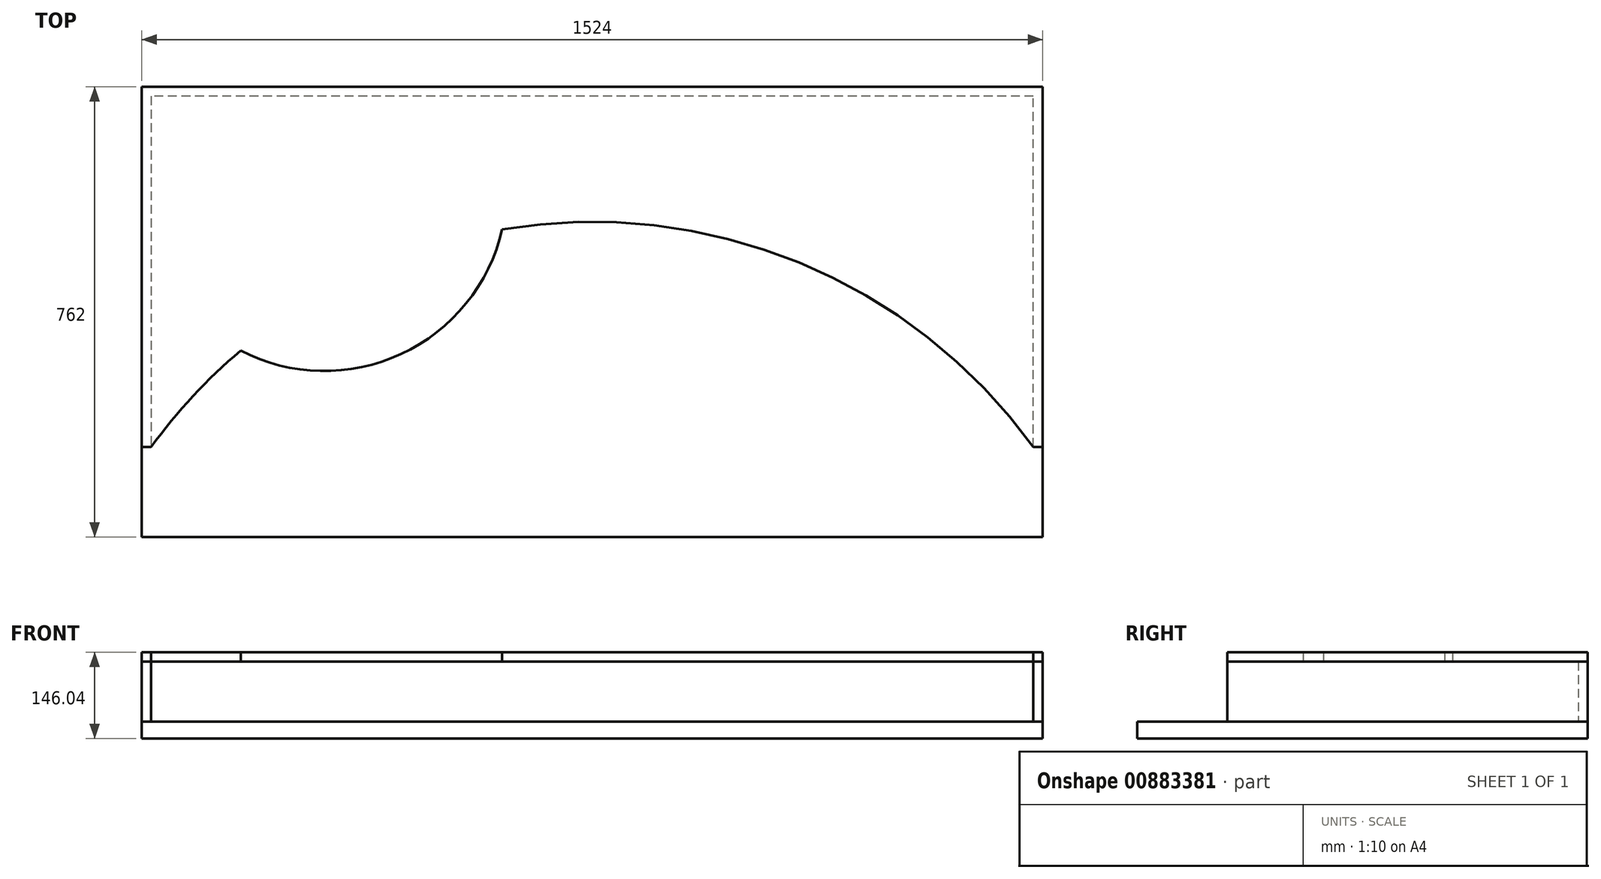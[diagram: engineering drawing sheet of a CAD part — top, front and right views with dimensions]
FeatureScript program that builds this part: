
annotation { "Feature Type Name" : "Feature", "Feature Type Description" : "" }
export const myFeature = defineFeature(function(context is Context, id is Id, definition is map)
    precondition{}
    {
        {
            var Q0;
            Q0=qCreatedBy(makeId("Top.planeOp"),FACE);
            var sketch = newSketch(context, id + "F0", { "sketchPlane" : qUnion([Q0])});
            skLineSegment(sketch, "E0.bottom", {"start": v(762, 381) * mm, "end": v(-762, 381) * mm});
            skLineSegment(sketch, "E0.top", {"start": v(762, -381) * mm, "end": v(-762, -381) * mm});
            skLineSegment(sketch, "E0.left", {"start": v(762, 381) * mm, "end": v(762, -381) * mm});
            skLineSegment(sketch, "E0.right", {"start": v(-762, 381) * mm, "end": v(-762, -381) * mm});
            skPoint(sketch, "E0.middle", {"position": v(0, 0) * mm});
            skSolve(sketch);
        }
        {
            var Q0;
            Q0 = qSketchRegion(id + "F0", true);
            extrude(context, id + "F1", {"entities" : qUnion([Q0]), "oppositeDirection" : true, "depth" : 28.57 * mm, "offsetDistance" : 25.4 * mm});
        }
        {
            var Q0;
            Q0=makeQuery(id+"F1.opExtrude","CAP_FACE",FACE,{"disambiguationData":[OSD([sQuery(id+"F0.wireOp",EDGE,"E0.bottom"),sQuery(id+"F0.wireOp",EDGE,"E0.top"),sQuery(id+"F0.wireOp",EDGE,"E0.left"),sQuery(id+"F0.wireOp",EDGE,"E0.right")])],"isStart":true});
            var sketch = newSketch(context, id + "F2", { "sketchPlane" : qUnion([Q0])});
            skLineSegment(sketch, "E1.bottom", {"start": v(-762, 381) * mm, "end": v(-746.13, 381) * mm});
            skLineSegment(sketch, "E1.top", {"start": v(-762, -228.6) * mm, "end": v(-746.13, -228.6) * mm});
            skLineSegment(sketch, "E1.left", {"start": v(-762, 381) * mm, "end": v(-762, -228.6) * mm});
            skLineSegment(sketch, "E1.right", {"start": v(-746.13, 381) * mm, "end": v(-746.13, -228.6) * mm});
            skLineSegment(sketch, "E2.bottom", {"start": v(762, -228.6) * mm, "end": v(746.12, -228.6) * mm});
            skLineSegment(sketch, "E2.top", {"start": v(762, 381) * mm, "end": v(746.12, 381) * mm});
            skLineSegment(sketch, "E2.left", {"start": v(762, -228.6) * mm, "end": v(762, 381) * mm});
            skLineSegment(sketch, "E2.right", {"start": v(746.13, -228.6) * mm, "end": v(746.12, 381) * mm});
            skLineSegment(sketch, "E3.bottom", {"start": v(746.12, 381) * mm, "end": v(-746.13, 381) * mm});
            skLineSegment(sketch, "E3.top", {"start": v(746.12, 365.12) * mm, "end": v(-746.13, 365.12) * mm});
            skLineSegment(sketch, "E3.left", {"start": v(746.12, 381) * mm, "end": v(746.12, 365.12) * mm});
            skLineSegment(sketch, "E3.right", {"start": v(-746.13, 381) * mm, "end": v(-746.13, 365.12) * mm});
            skSolve(sketch);
        }
        {
            var Q0;
            Q0 = qSketchRegion(id + "F2", true);
            extrude(context, id + "F3", {"entities" : qUnion([Q0]), "depth" : 101.6 * mm, "offsetDistance" : 25.4 * mm});
        }
        {
            var Q0;
            Q0=makeQuery(id+"F3.opExtrude","CAP_FACE",FACE,{"disambiguationData":[OSD([sQuery(id+"F2.wireOp",EDGE,"E1.bottom"),sQuery(id+"F2.wireOp",EDGE,"E1.top"),sQuery(id+"F2.wireOp",EDGE,"E1.left"),sQuery(id+"F2.wireOp",EDGE,"E1.right"),sQuery(id+"F2.wireOp",EDGE,"E2.bottom"),sQuery(id+"F2.wireOp",EDGE,"E2.top"),sQuery(id+"F2.wireOp",EDGE,"E2.left"),sQuery(id+"F2.wireOp",EDGE,"E2.right"),sQuery(id+"F2.wireOp",EDGE,"E3.bottom"),sQuery(id+"F2.wireOp",EDGE,"E3.top")])],"isStart":false});
            var sketch = newSketch(context, id + "F4", { "sketchPlane" : qUnion([Q0])});
            skArc(sketch, "E4", {"start": v(746.12, -228.6) * mm, "mid": v(0, 152.4) * mm, "end": v(-746.13, -228.6) * mm});
            skLineSegment(sketch, "E5.0", {"start": v(762, -381) * mm, "end": v(-762, -381) * mm, "construction": true});
            skLineSegment(sketch, "E6", {"start": v(457.2, -381) * mm, "end": v(457.2, -76.2) * mm, "construction": true});
            skLineSegment(sketch, "E7", {"start": v(-152.4, -381) * mm, "end": v(-152.4, 50.8) * mm, "construction": true});
            skLineSegment(sketch, "E8", {"start": v(-482.6, -381) * mm, "end": v(-482.6, -177.8) * mm, "construction": true});
            skSolve(sketch);
        }
        {
            var Q0;
            Q0=makeQuery(id+"F4.imprint","IMPRINT",FACE,{"disambiguationData":[TD([[makeQuery(id+"F4.imprint","IMPRINT",EDGE,{"derivedFrom":sQuery(id+"F4.wireOp",EDGE,"E4")}),-1.0]])]});
            var Q1;
            Q1=makeQuery(id+"F4.imprint","IMPRINT",FACE,{"disambiguationData":[TD([[makeQuery(id+"F4.imprint","IMPRINT",EDGE,{"derivedFrom":makeQuery(id+"F3.opExtrude","CAP_EDGE",EDGE,{"disambiguationData":[OSD([sQuery(id+"F2.wireOp",EDGE,"E1.top")])],"isStart":false})}),1.0]])]});
            extrude(context, id + "F5", {"entities" : qUnion([Q0, Q1]), "depth" : 15.88 * mm, "offsetDistance" : 25.4 * mm});
        }
        {
            var Q0;
            Q0=makeQuery(id+"F5.opExtrude","CAP_FACE",FACE,{"disambiguationData":[OSD([sQuery(id+"F2.wireOp",EDGE,"E1.bottom"),sQuery(id+"F2.wireOp",EDGE,"E1.top"),sQuery(id+"F2.wireOp",EDGE,"E1.left"),sQuery(id+"F2.wireOp",EDGE,"E2.bottom"),sQuery(id+"F2.wireOp",EDGE,"E2.top"),sQuery(id+"F2.wireOp",EDGE,"E2.left"),sQuery(id+"F2.wireOp",EDGE,"E3.bottom"),sQuery(id+"F4.wireOp",EDGE,"E4")])],"isStart":false});
            var sketch = newSketch(context, id + "F6", { "sketchPlane" : qUnion([Q0])});
            skLineSegment(sketch, "E9.bottom", {"start": v(247.65, 228.6) * mm, "end": v(-247.65, 228.6) * mm});
            skLineSegment(sketch, "E9.top", {"start": v(247.65, 254) * mm, "end": v(-247.65, 254) * mm});
            skLineSegment(sketch, "E9.left", {"start": v(247.65, 228.6) * mm, "end": v(247.65, 254) * mm});
            skLineSegment(sketch, "E9.right", {"start": v(-247.65, 228.6) * mm, "end": v(-247.65, 254) * mm});
            skPoint(sketch, "E9.middle", {"position": v(0, 241.3) * mm});
            skLineSegment(sketch, "E10", {"start": v(247.65, 228.6) * mm, "end": v(700.33, 27.59) * mm});
            skLineSegment(sketch, "E11", {"start": v(700.33, 27.59) * mm, "end": v(710.63, 50.8) * mm});
            skLineSegment(sketch, "E12", {"start": v(710.63, 50.8) * mm, "end": v(257.96, 251.81) * mm});
            skLineSegment(sketch, "E13", {"start": v(257.96, 251.81) * mm, "end": v(247.65, 228.6) * mm});
            skLineSegment(sketch, "E14", {"start": v(-286.94, 228.6) * mm, "end": v(-635, 73.63) * mm});
            skLineSegment(sketch, "E15", {"start": v(-635, 73.63) * mm, "end": v(-531.69, -158.4) * mm});
            skLineSegment(sketch, "E16", {"start": v(-531.69, -158.4) * mm, "end": v(-183.63, -3.44) * mm});
            skLineSegment(sketch, "E17", {"start": v(-183.63, -3.44) * mm, "end": v(-286.94, 228.6) * mm});
            skArc(sketch, "E18", {"start": v(-594.99, -65.56) * mm, "mid": v(-323.41, -71.35) * mm, "end": v(-152.4, 139.7) * mm});
            skSolve(sketch);
        }
        {
            var Q0;
            {var subQ0=sQuery(id+"F6.wireOp",EDGE,"E18");var subQ1=sQuery(id+"F6.wireOp",EDGE,"E15");var subQ2=makeQuery(id+"F6.imprint","INTERSECT",VERTEX,{"derivedFrom":[subQ1,subQ0]});Q0=makeQuery(id+"F6.imprint","IMPRINT",FACE,{"disambiguationData":[TD([[makeQuery(id+"F6.imprint","IMPRINT",EDGE,{"disambiguationData":[TD([[subQ2,1.0]])],"derivedFrom":subQ1}),-1.0]])]});}
            var Q1;
            {var subQ0=sQuery(id+"F6.wireOp",EDGE,"E18");var subQ1=sQuery(id+"F6.wireOp",EDGE,"E15");var subQ2=makeQuery(id+"F6.imprint","INTERSECT",VERTEX,{"derivedFrom":[subQ1,subQ0]});Q1=makeQuery(id+"F6.imprint","IMPRINT",FACE,{"disambiguationData":[TD([[makeQuery(id+"F6.imprint","IMPRINT",EDGE,{"disambiguationData":[TD([[subQ2,1.0]])],"derivedFrom":subQ1}),1.0]])]});}
            var Q2;
            {var subQ0=sQuery(id+"F6.wireOp",EDGE,"E18");var subQ1=sQuery(id+"F6.wireOp",EDGE,"E17");var subQ2=makeQuery(id+"F6.imprint","INTERSECT",VERTEX,{"derivedFrom":[subQ1,subQ0]});Q2=makeQuery(id+"F6.imprint","IMPRINT",FACE,{"disambiguationData":[TD([[makeQuery(id+"F6.imprint","IMPRINT",EDGE,{"disambiguationData":[TD([[subQ2,-1.0]])],"derivedFrom":subQ1}),-1.0]])]});}
            var Q3;
            {var subQ0=sQuery(id+"F6.wireOp",EDGE,"E18");var subQ1=sQuery(id+"F6.wireOp",EDGE,"E16");var subQ2=makeQuery(id+"F6.imprint","INTERSECT",VERTEX,{"disambiguationData":[OD(0.0)],"derivedFrom":[subQ1,subQ0]});Q3=makeQuery(id+"F6.imprint","IMPRINT",FACE,{"disambiguationData":[TD([[makeQuery(id+"F6.imprint","IMPRINT",EDGE,{"disambiguationData":[TD([[subQ2,-1.0]])],"derivedFrom":subQ1}),-1.0]])]});}
            var Q4;
            Q4=makeQuery(id+"F5.opExtrude","CAP_FACE",FACE,{"disambiguationData":[OSD([sQuery(id+"F2.wireOp",EDGE,"E1.bottom"),sQuery(id+"F2.wireOp",EDGE,"E1.top"),sQuery(id+"F2.wireOp",EDGE,"E1.left"),sQuery(id+"F2.wireOp",EDGE,"E2.bottom"),sQuery(id+"F2.wireOp",EDGE,"E2.top"),sQuery(id+"F2.wireOp",EDGE,"E2.left"),sQuery(id+"F2.wireOp",EDGE,"E3.bottom"),sQuery(id+"F4.wireOp",EDGE,"E4")])],"isStart":true});
            extrude(context, id + "F7", {"entities" : qUnion([Q0, Q1, Q2, Q3]), "operationType" : NewBodyOperationType.ADD, "endBound" : BoundingType.UP_TO_SURFACE, "oppositeDirection" : true, "depth" : 25.4 * mm, "endBoundEntityFace" : qUnion([Q4]), "offsetDistance" : 25.4 * mm});
        }
    });
